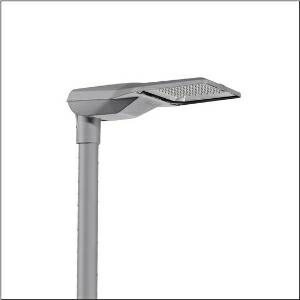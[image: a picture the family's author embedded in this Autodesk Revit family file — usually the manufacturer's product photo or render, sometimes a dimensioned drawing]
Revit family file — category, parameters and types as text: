
# Revit family: streetlight_sl_21_iq_midi___st1_0ab_5xe3m31d08mb_fee6
name_source: partatom
category: Lighting Fixtures
units: mm (PartAtom-declared; Revit-internal decimal feet)

## family parameters
Cut with Voids When Loaded = No
Host = Face
Light Source = No
Part Type = Normal
Room Calculation Point = No
Round Connector Dimension = Use Diameter
Shared = No

## types (1)
- --- (1 x LED, 17170 lm, 146.7 W, 3000K)
    Apparent Load = 147 VA
    CIE Flux Codes = 38 73 97 100 100
    Color Rendering = 70
    Color Temperature = 3000K
    Default Elevation = 1800 mm
    Description = Streetlight SL 21 iQ midi, mast luminaire, primary light control with lens, of PMMA, primary optical cover: cover, of toughened safety glass, transparent, light distribution: ST1.0aB, light emission: direct distribution, primary light characteristic: asymmetric, installation type: post-top, side-entry, LED, High Power LED, rated luminous flux: 17.170lm, luminous efficacy: 117lm/W, light colour: 730, colour temperature: 3000K, control gear: iQ-Comfort, control: Auto-Match, Temp-Guard, Lumen-Switch, Night-Set, Smart-Wire, Light-Fading, Desk-Remote (wireless, voltage-free reading and setting of iQ features in the workshop via application-optimized NFC function/RFID function), optimised constant luminous flux control (CLO 2.0), pre-setting: linear dimming characteristic, mains connection: 230..240V, AC, 50/60Hz, start of lifetime: 147W, end of service life: 161W, reduction: 62W, luminaire housing, of diecast aluminium, powder-coated, Siteco® metallic grey (DB 702S), corrosivity category C5 mid according to DIN EN ISO 12944, please order mast flange separately, inclination adjustable: 0°, 5°, 10°, 15°, sealing non-destructively replaceable, multi-level sealing system, length: 644mm, width: 335mm, height: 110mm, mast flange for spigot size: 42mm (side-entry): 5XC10008XM4, 60/48mm (side-entry/post-top): 5XC10108XM2, 76/60mm (side-entry/post-top): 5XC10108XM1, mounting height: 4..8m, protection rating (complete): IP66, insulation class (complete): insulation class II (safety insulation), certification: CE, ENEC, ENEC+, VDE, impact resistance: IK10, permissible operating ambient temperature for outdoor applications: -40..+50°C, standard-compliant lighting for roads and squares, packaging unit: 1 piece

Light Distribution: ST1.0aB
    Height = 111 mm
    Lamp = 1 x LED
    Lamp Light Flux = 17170 lm
    Lamp Power = 146.7 W
    Lamp count = 1
    Length = 644 mm
    Luminous efficacy = 117 lm/W
    Manufacturer = Siteco
    ModVariant = No
    Model = 5XE3M31D08MB
    Number of Poles = 1
    OnlyDefault = Yes
    Power Factor = 1
    Product Name = Streetlight SL 21 iQ midi | ST1.0aB
    Product group = mast luminaire | pylon top
    ProductGroupID = 6100
    Protection Class = Protection class II
    Protection Degree = IP 66
    RLX_Detail_Level = 1
    RLX_Emergency_Light_Flux = 0 lm
    RLX_Emergency_Type = 0
    RLX_Emergency_Type_DB = No
    RlxData = <blob elided: 26981 chars, md5=1244bd0b>
    Socket = socket
    Standby Power = 0 W
    System Light Flux = 17170 lm
    System Power = 147 W
    Type Comments = factory setting: luminous flux: 100 % | dim-lin: 254 | 753 mA
    Type Image = l_1004298.jpg
    URL = http://relux.com
    VarID = @adj_183034
    Voltage = 0 V
    Weight = 0.00 kg
    Width = 336 mm

## geometry (parser evidence)
native form markers: Blend x4, Sweep x11
no freeform markers — native parametric forms only
